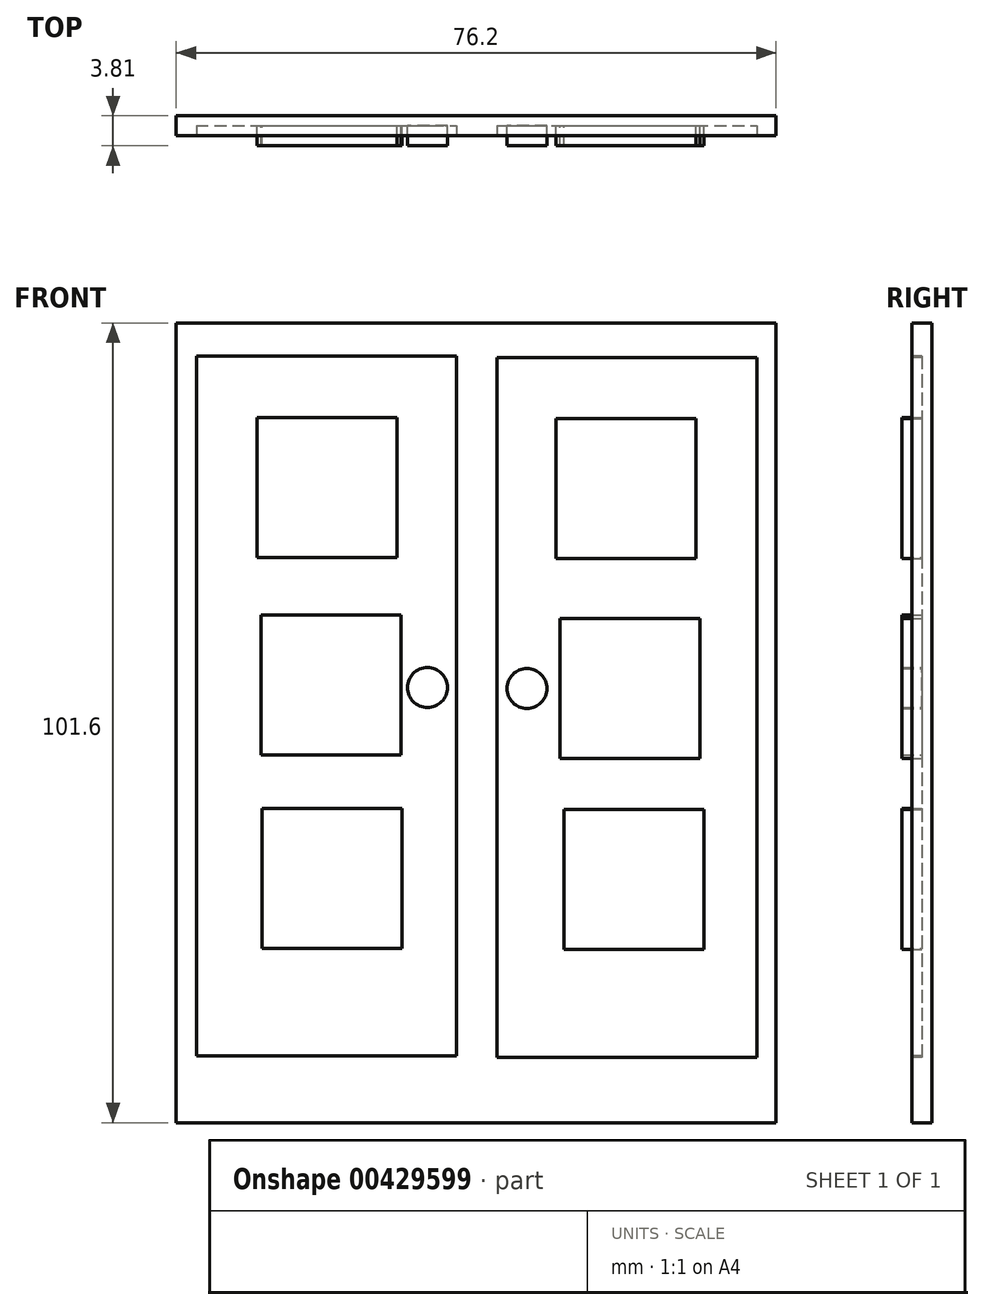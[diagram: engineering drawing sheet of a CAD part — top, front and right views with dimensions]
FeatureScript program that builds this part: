
annotation { "Feature Type Name" : "Feature", "Feature Type Description" : "" }
export const myFeature = defineFeature(function(context is Context, id is Id, definition is map)
    precondition{}
    {
        {
            var Q0;
            Q0=qCreatedBy(makeId("Front.planeOp"),FACE);
            var sketch = newSketch(context, id + "F0", { "sketchPlane" : qUnion([Q0])});
            skLineSegment(sketch, "E0.bottom", {"start": v(-36.76, -60.42) * mm, "end": v(39.44, -60.42) * mm});
            skLineSegment(sketch, "E0.top", {"start": v(-36.76, 41.18) * mm, "end": v(39.44, 41.18) * mm});
            skLineSegment(sketch, "E0.left", {"start": v(-36.76, -60.42) * mm, "end": v(-36.76, 41.18) * mm});
            skLineSegment(sketch, "E0.right", {"start": v(39.44, -60.42) * mm, "end": v(39.44, 41.18) * mm});
            skSolve(sketch);
        }
        {
            var Q0;
            Q0 = qSketchRegion(id + "F0", true);
            extrude(context, id + "F1", {"entities" : qUnion([Q0]), "depth" : 2.54 * mm});
        }
        {
            var Q0;
            Q0=makeQuery(id+"F1.opExtrude","CAP_FACE",FACE,{"disambiguationData":[OSD([sQuery(id+"F0.wireOp",EDGE,"E0.bottom"),sQuery(id+"F0.wireOp",EDGE,"E0.top"),sQuery(id+"F0.wireOp",EDGE,"E0.left"),sQuery(id+"F0.wireOp",EDGE,"E0.right")])],"isStart":false});
            var sketch = newSketch(context, id + "F2", { "sketchPlane" : qUnion([Q0])});
            skLineSegment(sketch, "E1.bottom", {"start": v(-34.19, 36.95) * mm, "end": v(-1.17, 36.95) * mm});
            skLineSegment(sketch, "E1.top", {"start": v(-34.19, -51.95) * mm, "end": v(-1.17, -51.95) * mm});
            skLineSegment(sketch, "E1.left", {"start": v(-34.19, 36.95) * mm, "end": v(-34.19, -51.95) * mm});
            skLineSegment(sketch, "E1.right", {"start": v(-1.17, 36.95) * mm, "end": v(-1.17, -51.95) * mm});
            skLineSegment(sketch, "E2.bottom", {"start": v(4.02, 36.78) * mm, "end": v(37.04, 36.78) * mm});
            skLineSegment(sketch, "E2.top", {"start": v(4.02, -52.12) * mm, "end": v(37.04, -52.12) * mm});
            skLineSegment(sketch, "E2.left", {"start": v(4.02, 36.78) * mm, "end": v(4.02, -52.12) * mm});
            skLineSegment(sketch, "E2.right", {"start": v(37.04, 36.78) * mm, "end": v(37.04, -52.12) * mm});
            skSolve(sketch);
        }
        {
            var Q0;
            Q0 = qSketchRegion(id + "F2", true);
            extrude(context, id + "F3", {"entities" : qUnion([Q0]), "operationType" : NewBodyOperationType.REMOVE, "oppositeDirection" : true, "depth" : 1.27 * mm});
        }
        {
            var Q0;
            Q0=makeQuery(id+"F3.boolean.opBoolean","COPY",FACE,{"derivedFrom":makeQuery(id+"F3.opExtrude","CAP_FACE",FACE,{"disambiguationData":[OSD([sQuery(id+"F2.wireOp",EDGE,"E1.bottom"),sQuery(id+"F2.wireOp",EDGE,"E1.top"),sQuery(id+"F2.wireOp",EDGE,"E1.left"),sQuery(id+"F2.wireOp",EDGE,"E1.right")])],"isStart":false})});
            var sketch = newSketch(context, id + "F4", { "sketchPlane" : qUnion([Q0])});
            skLineSegment(sketch, "E3.bottom", {"start": v(-26.51, 29.17) * mm, "end": v(-8.73, 29.17) * mm});
            skLineSegment(sketch, "E3.top", {"start": v(-26.51, 11.4) * mm, "end": v(-8.73, 11.4) * mm});
            skLineSegment(sketch, "E3.left", {"start": v(-26.51, 29.17) * mm, "end": v(-26.51, 11.4) * mm});
            skLineSegment(sketch, "E3.right", {"start": v(-8.73, 29.17) * mm, "end": v(-8.73, 11.4) * mm});
            skLineSegment(sketch, "E4.bottom", {"start": v(-25.96, 4.06) * mm, "end": v(-8.18, 4.06) * mm});
            skLineSegment(sketch, "E4.top", {"start": v(-25.96, -13.72) * mm, "end": v(-8.18, -13.72) * mm});
            skLineSegment(sketch, "E4.left", {"start": v(-25.96, 4.06) * mm, "end": v(-25.96, -13.72) * mm});
            skLineSegment(sketch, "E4.right", {"start": v(-8.18, 4.06) * mm, "end": v(-8.18, -13.72) * mm});
            skLineSegment(sketch, "E5.bottom", {"start": v(-25.85, -20.52) * mm, "end": v(-8.07, -20.52) * mm});
            skLineSegment(sketch, "E5.top", {"start": v(-25.85, -38.3) * mm, "end": v(-8.07, -38.3) * mm});
            skLineSegment(sketch, "E5.left", {"start": v(-25.85, -20.52) * mm, "end": v(-25.85, -38.3) * mm});
            skLineSegment(sketch, "E5.right", {"start": v(-8.07, -20.52) * mm, "end": v(-8.07, -38.3) * mm});
            skLineSegment(sketch, "E6.bottom", {"start": v(11.5, 29.02) * mm, "end": v(29.28, 29.02) * mm});
            skLineSegment(sketch, "E6.top", {"start": v(11.5, 11.24) * mm, "end": v(29.28, 11.24) * mm});
            skLineSegment(sketch, "E6.left", {"start": v(11.5, 29.02) * mm, "end": v(11.5, 11.24) * mm});
            skLineSegment(sketch, "E6.right", {"start": v(29.28, 29.02) * mm, "end": v(29.28, 11.24) * mm});
            skLineSegment(sketch, "E7.bottom", {"start": v(12.02, 3.63) * mm, "end": v(29.8, 3.63) * mm});
            skLineSegment(sketch, "E7.top", {"start": v(12.02, -14.15) * mm, "end": v(29.8, -14.15) * mm});
            skLineSegment(sketch, "E7.left", {"start": v(12.02, 3.63) * mm, "end": v(12.02, -14.15) * mm});
            skLineSegment(sketch, "E7.right", {"start": v(29.8, 3.63) * mm, "end": v(29.8, -14.15) * mm});
            skLineSegment(sketch, "E8.bottom", {"start": v(12.5, -20.61) * mm, "end": v(30.29, -20.61) * mm});
            skLineSegment(sketch, "E8.top", {"start": v(12.5, -38.4) * mm, "end": v(30.29, -38.4) * mm});
            skLineSegment(sketch, "E8.left", {"start": v(12.5, -20.61) * mm, "end": v(12.5, -38.4) * mm});
            skLineSegment(sketch, "E8.right", {"start": v(30.29, -20.61) * mm, "end": v(30.29, -38.4) * mm});
            skSolve(sketch);
        }
        {
            var Q0;
            Q0 = qSketchRegion(id + "F4", true);
            extrude(context, id + "F5", {"entities" : qUnion([Q0]), "operationType" : NewBodyOperationType.ADD, "depth" : 2.54 * mm});
        }
        {
            var Q0;
            Q0=makeQuery(id+"F3.boolean.opBoolean","COPY",FACE,{"derivedFrom":makeQuery(id+"F3.opExtrude","CAP_FACE",FACE,{"disambiguationData":[OSD([sQuery(id+"F2.wireOp",EDGE,"E2.bottom"),sQuery(id+"F2.wireOp",EDGE,"E2.top"),sQuery(id+"F2.wireOp",EDGE,"E2.left"),sQuery(id+"F2.wireOp",EDGE,"E2.right")])],"isStart":false})});
            var sketch = newSketch(context, id + "F6", { "sketchPlane" : qUnion([Q0])});
            skCircle(sketch, "E9", {"center": v(-4.85, -5.15) * mm, "radius": 2.54 * mm});
            skCircle(sketch, "E10", {"center": v(7.8, -5.26) * mm, "radius": 2.54 * mm});
            skPoint(sketch, "E10.centerSnap0", {"position": v(12.02, -5.26) * mm});
            skSolve(sketch);
        }
        {
            var Q0;
            Q0 = qSketchRegion(id + "F6", true);
            extrude(context, id + "F7", {"entities" : qUnion([Q0]), "operationType" : NewBodyOperationType.ADD, "depth" : 2.54 * mm});
        }
    });
